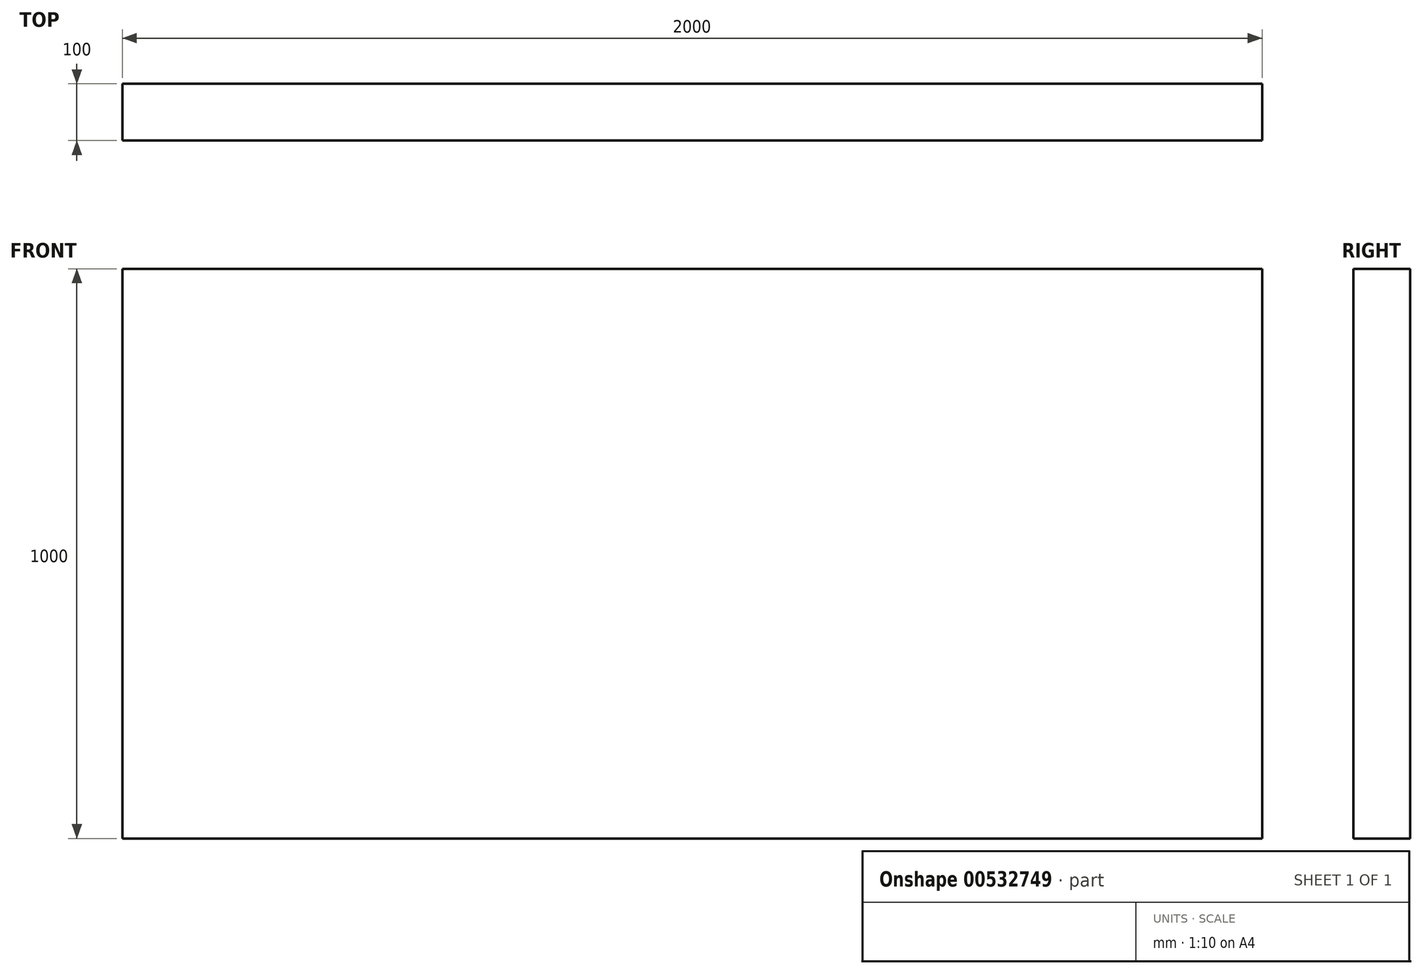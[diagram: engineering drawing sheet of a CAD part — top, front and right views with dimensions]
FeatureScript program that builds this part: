
annotation { "Feature Type Name" : "Feature", "Feature Type Description" : "" }
export const myFeature = defineFeature(function(context is Context, id is Id, definition is map)
    precondition{}
    {
        {
            var Q0;
            Q0=qCreatedBy(makeId("Front.planeOp"),FACE);
            var sketch = newSketch(context, id + "F0", { "sketchPlane" : qUnion([Q0])});
            skLineSegment(sketch, "E0.bottom", {"start": v(0, 0) * mm, "end": v(2000, 0) * mm});
            skLineSegment(sketch, "E0.top", {"start": v(0, 1000) * mm, "end": v(2000, 1000) * mm});
            skLineSegment(sketch, "E0.left", {"start": v(0, 0) * mm, "end": v(0, 1000) * mm});
            skLineSegment(sketch, "E0.right", {"start": v(2000, 0) * mm, "end": v(2000, 1000) * mm});
            skSolve(sketch);
        }
        {
            var Q0;
            Q0=makeQuery(id+"F0.imprint","IMPRINT",FACE,{"disambiguationData":[TD([[makeQuery(id+"F0.imprint","IMPRINT",EDGE,{"derivedFrom":sQuery(id+"F0.wireOp",EDGE,"E0.bottom")}),1.0]])]});
            extrude(context, id + "F1", {"entities" : qUnion([Q0]), "oppositeDirection" : true, "depth" : 100 * mm, "offsetDistance" : 25 * mm});
        }
    });
